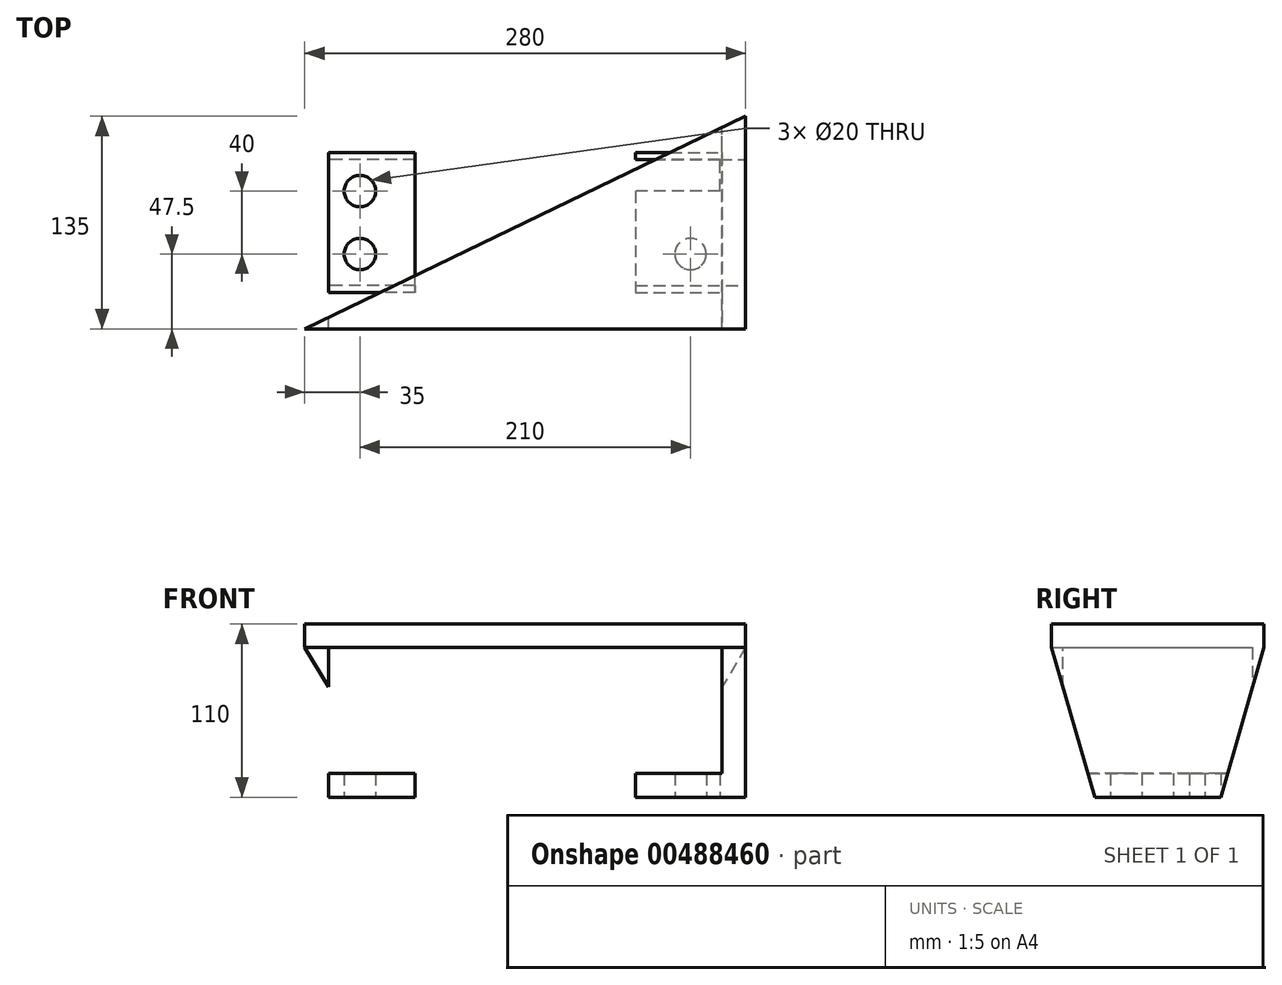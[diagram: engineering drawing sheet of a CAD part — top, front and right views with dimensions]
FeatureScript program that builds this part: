
annotation { "Feature Type Name" : "Feature", "Feature Type Description" : "" }
export const myFeature = defineFeature(function(context is Context, id is Id, definition is map)
    precondition{}
    {
        {
            var Q0;
            Q0=qCreatedBy(makeId("Top.planeOp"),FACE);
            var sketch = newSketch(context, id + "F0", { "sketchPlane" : qUnion([Q0])});
            skLineSegment(sketch, "E0", {"start": v(0, 0) * mm, "end": v(0, 135) * mm});
            skLineSegment(sketch, "E1", {"start": v(0, 135) * mm, "end": v(280, 135) * mm});
            skLineSegment(sketch, "E2", {"start": v(280, 135) * mm, "end": v(280, 0) * mm});
            skLineSegment(sketch, "E3", {"start": v(280, 0) * mm, "end": v(0, 0) * mm});
            skSolve(sketch);
        }
        {
            var Q0;
            Q0 = qSketchRegion(id + "F0", true);
            extrude(context, id + "F1", {"entities" : qUnion([Q0]), "depth" : 15 * mm});
        }
        {
            var Q0;
            Q0=makeQuery(id+"F1.opExtrude","SWEPT_FACE",FACE,{"disambiguationData":[OSD([sQuery(id+"F0.wireOp",EDGE,"E0")])]});
            var sketch = newSketch(context, id + "F2", { "sketchPlane" : qUnion([Q0])});
            skLineSegment(sketch, "E4", {"start": v(-135, 0) * mm, "end": v(0, 0) * mm});
            skLineSegment(sketch, "E5", {"start": v(-135, 15) * mm, "end": v(-166.77, 15) * mm});
            skLineSegment(sketch, "E6", {"start": v(-166.77, 15) * mm, "end": v(-166.77, -95) * mm});
            skLineSegment(sketch, "E7", {"start": v(-67.5, -95) * mm, "end": v(-27.5, -95) * mm});
            skLineSegment(sketch, "E8", {"start": v(-67.5, -95) * mm, "end": v(-107.5, -95) * mm});
            skLineSegment(sketch, "E9", {"start": v(-107.5, -95) * mm, "end": v(-135, 0) * mm});
            skLineSegment(sketch, "E10", {"start": v(-27.5, -95) * mm, "end": v(0, 0) * mm});
            skPoint(sketch, "E11.start.orphan", {"position": v(-67.5, 0) * mm});
            skSolve(sketch);
        }
        {
            var Q0;
            Q0 = qSketchRegion(id + "F2", true);
            extrude(context, id + "F3", {"entities" : qUnion([Q0]), "operationType" : NewBodyOperationType.ADD, "oppositeDirection" : true, "depth" : 15 * mm});
        }
        {
            var Q0;
            Q0=makeQuery(id+"F1.opExtrude","SWEPT_FACE",FACE,{"disambiguationData":[OSD([sQuery(id+"F0.wireOp",EDGE,"E2")])]});
            var sketch = newSketch(context, id + "F4", { "sketchPlane" : qUnion([Q0])});
            skLineSegment(sketch, "E12", {"start": v(0, 15) * mm, "end": v(-22.22, 15) * mm});
            skLineSegment(sketch, "E13", {"start": v(-22.22, 15) * mm, "end": v(-22.22, -95) * mm});
            skLineSegment(sketch, "E14", {"start": v(67.5, -95) * mm, "end": v(107.5, -95) * mm});
            skLineSegment(sketch, "E15", {"start": v(67.5, -95) * mm, "end": v(27.5, -95) * mm});
            skLineSegment(sketch, "E16", {"start": v(27.5, -95) * mm, "end": v(0, 0) * mm});
            skLineSegment(sketch, "E17", {"start": v(107.5, -95) * mm, "end": v(135, 0) * mm});
            skPoint(sketch, "E18.orphan", {"position": v(67.5, 0) * mm});
            skLineSegment(sketch, "E19", {"start": v(0, 0) * mm, "end": v(0, 15) * mm});
            skLineSegment(sketch, "E20", {"start": v(135, 15) * mm, "end": v(135, 0) * mm});
            skLineSegment(sketch, "E21", {"start": v(107.5, -95) * mm, "end": v(27.5, -95) * mm});
            skSolve(sketch);
        }
        {
            var Q0;
            Q0=makeQuery(id+"F4.imprint","IMPRINT",FACE,{"disambiguationData":[TD([[makeQuery(id+"F4.imprint","IMPRINT",EDGE,{"derivedFrom":sQuery(id+"F4.wireOp",EDGE,"E16")}),-1.0]])]});
            var Q1;
            Q1=makeQuery(id+"F4.imprint","IMPRINT",FACE,{"disambiguationData":[TD([[makeQuery(id+"F4.imprint","IMPRINT",EDGE,{"derivedFrom":sQuery(id+"F4.wireOp",EDGE,"E20")}),-1.0]])]});
            extrude(context, id + "F5", {"entities" : qUnion([Q0, Q1]), "operationType" : NewBodyOperationType.ADD, "oppositeDirection" : true, "depth" : 15 * mm});
        }
        {
            var Q0;
            Q0=makeQuery(id+"F1.opExtrude","CAP_FACE",FACE,{"disambiguationData":[OSD([sQuery(id+"F0.wireOp",EDGE,"E0"),sQuery(id+"F0.wireOp",EDGE,"E1"),sQuery(id+"F0.wireOp",EDGE,"E2"),sQuery(id+"F0.wireOp",EDGE,"E3")])],"isStart":false});
            var sketch = newSketch(context, id + "F6", { "sketchPlane" : qUnion([Q0])});
            skLineSegment(sketch, "E22", {"start": v(280, 0) * mm, "end": v(0, 135) * mm});
            skLineSegment(sketch, "E23", {"start": v(0, 135) * mm, "end": v(0, 0) * mm});
            skLineSegment(sketch, "E24", {"start": v(0, 0) * mm, "end": v(280, 135) * mm});
            skCircle(sketch, "E25", {"center": v(140, 67.5) * mm, "radius": 30 * mm});
            skSolve(sketch);
        }
        {
            var Q0;
            {var subQ0=sQuery(id+"F6.wireOp",EDGE,"E25");var subQ1=sQuery(id+"F6.wireOp",EDGE,"E22");var subQ2=makeQuery(id+"F6.imprint","INTERSECT",VERTEX,{"disambiguationData":[OD(0.0)],"derivedFrom":[subQ1,subQ0]});Q0=makeQuery(id+"F6.imprint","IMPRINT",FACE,{"disambiguationData":[TD([[makeQuery(id+"F6.imprint","IMPRINT",EDGE,{"disambiguationData":[TD([[subQ2,-1.0]])],"derivedFrom":subQ1}),1.0]])]});}
            var Q1;
            {var subQ0=sQuery(id+"F6.wireOp",EDGE,"E25");var subQ1=sQuery(id+"F6.wireOp",EDGE,"E22");var subQ2=makeQuery(id+"F6.imprint","INTERSECT",VERTEX,{"disambiguationData":[OD(0.0)],"derivedFrom":[subQ1,subQ0]});Q1=makeQuery(id+"F6.imprint","IMPRINT",FACE,{"disambiguationData":[TD([[makeQuery(id+"F6.imprint","IMPRINT",EDGE,{"disambiguationData":[TD([[subQ2,-1.0]])],"derivedFrom":subQ1}),-1.0]])]});}
            var Q2;
            {var subQ0=sQuery(id+"F6.wireOp",EDGE,"E24");var subQ1=sQuery(id+"F6.wireOp",EDGE,"E22");var subQ2=makeQuery(id+"F6.imprint","INTERSECT",VERTEX,{"derivedFrom":[subQ1,subQ0]});Q2=makeQuery(id+"F6.imprint","IMPRINT",FACE,{"disambiguationData":[TD([[makeQuery(id+"F6.imprint","IMPRINT",EDGE,{"disambiguationData":[TD([[subQ2,-1.0]])],"derivedFrom":subQ1}),1.0]])]});}
            var Q3;
            {var subQ0=sQuery(id+"F6.wireOp",EDGE,"E24");var subQ1=sQuery(id+"F6.wireOp",EDGE,"E22");var subQ2=makeQuery(id+"F6.imprint","INTERSECT",VERTEX,{"derivedFrom":[subQ1,subQ0]});Q3=makeQuery(id+"F6.imprint","IMPRINT",FACE,{"disambiguationData":[TD([[makeQuery(id+"F6.imprint","IMPRINT",EDGE,{"disambiguationData":[TD([[subQ2,-1.0]])],"derivedFrom":subQ1}),-1.0]])]});}
            extrude(context, id + "F7", {"entities" : qUnion([Q0, Q1, Q2, Q3]), "operationType" : NewBodyOperationType.REMOVE, "endBound" : BoundingType.THROUGH_ALL, "oppositeDirection" : true, "depth" : 25 * mm});
        }
        {
            var Q0;
            Q0=makeQuery(id+"F3.opExtrude","CAP_FACE",FACE,{"disambiguationData":[OSD([sQuery(id+"F2.wireOp",EDGE,"E4"),sQuery(id+"F2.wireOp",EDGE,"E7"),sQuery(id+"F2.wireOp",EDGE,"E8"),sQuery(id+"F2.wireOp",EDGE,"E9"),sQuery(id+"F2.wireOp",EDGE,"E10")])],"isStart":false});
            var sketch = newSketch(context, id + "F8", { "sketchPlane" : qUnion([Q0])});
            skLineSegment(sketch, "E26", {"start": v(27.5, -80) * mm, "end": v(111.84, -80) * mm});
            skLineSegment(sketch, "E27", {"start": v(111.84, -80) * mm, "end": v(23.16, -80) * mm});
            skLineSegment(sketch, "E28", {"start": v(27.5, -95) * mm, "end": v(23.16, -80) * mm});
            skLineSegment(sketch, "E29", {"start": v(27.5, -95) * mm, "end": v(107.5, -95) * mm});
            skLineSegment(sketch, "E30", {"start": v(107.5, -95) * mm, "end": v(111.84, -80) * mm});
            skSolve(sketch);
        }
        {
            var Q0;
            Q0 = qSketchRegion(id + "F8", true);
            extrude(context, id + "F9", {"entities" : qUnion([Q0]), "operationType" : NewBodyOperationType.ADD, "depth" : (70 - 15) * mm});
        }
        {
            var Q0;
            Q0=makeQuery(id+"F5.opExtrude","CAP_FACE",FACE,{"disambiguationData":[OSD([sQuery(id+"F0.wireOp",EDGE,"E2"),sQuery(id+"F4.wireOp",EDGE,"E16"),sQuery(id+"F4.wireOp",EDGE,"E17"),sQuery(id+"F4.wireOp",EDGE,"E20"),sQuery(id+"F4.wireOp",EDGE,"E21"),sQuery(id+"F4.wireOp",EDGE,"E19")])],"isStart":false});
            var sketch = newSketch(context, id + "F10", { "sketchPlane" : qUnion([Q0])});
            skLineSegment(sketch, "E31", {"start": v(-67.5, -95) * mm, "end": v(-67.5, -80) * mm});
            skLineSegment(sketch, "E32", {"start": v(-67.5, -80) * mm, "end": v(-23.16, -80) * mm});
            skLineSegment(sketch, "E33", {"start": v(-23.16, -80) * mm, "end": v(-111.84, -80) * mm});
            skLineSegment(sketch, "E34", {"start": v(-107.5, -95) * mm, "end": v(-27.5, -95) * mm});
            skLineSegment(sketch, "E35", {"start": v(-27.5, -95) * mm, "end": v(-23.16, -80) * mm});
            skLineSegment(sketch, "E36", {"start": v(-111.84, -80) * mm, "end": v(-107.5, -95) * mm});
            skSolve(sketch);
        }
        {
            var Q0;
            Q0 = qSketchRegion(id + "F10", true);
            extrude(context, id + "F11", {"entities" : qUnion([Q0]), "operationType" : NewBodyOperationType.ADD, "depth" : 55 * mm});
        }
        {
            var Q0;
            Q0=makeQuery(id+"F11.boolean.opBoolean","MERGE",FACE,{"derivedFrom":[makeQuery(id+"F5.opExtrude","SWEPT_FACE",FACE,{"disambiguationData":[OSD([sQuery(id+"F4.wireOp",EDGE,"E21")])]}),makeQuery(id+"F11.opExtrude","SWEPT_FACE",FACE,{"disambiguationData":[OSD([sQuery(id+"F10.wireOp",EDGE,"E34")])]})]});
            var sketch = newSketch(context, id + "F12", { "sketchPlane" : qUnion([Q0])});
            skLineSegment(sketch, "E37", {"start": v(210, -27.5) * mm, "end": v(280, -27.5) * mm});
            skLineSegment(sketch, "E38", {"start": v(245, -27.5) * mm, "end": v(245, -107.5) * mm});
            skLineSegment(sketch, "E39", {"start": v(245, -67.5) * mm, "end": v(263.69, -67.5) * mm});
            skLineSegment(sketch, "E40", {"start": v(263.69, -27.5) * mm, "end": v(263.69, -67.5) * mm});
            skLineSegment(sketch, "E41", {"start": v(263.69, -67.5) * mm, "end": v(263.69, -107.5) * mm});
            skLineSegment(sketch, "E42", {"start": v(263.69, -47.5) * mm, "end": v(0, -47.5) * mm});
            skLineSegment(sketch, "E43", {"start": v(263.69, -87.5) * mm, "end": v(0, -87.5) * mm});
            skLineSegment(sketch, "E44", {"start": v(280, -27.5) * mm, "end": v(0, -27.5) * mm});
            skLineSegment(sketch, "E45", {"start": v(0, -27.5) * mm, "end": v(0, -107.5) * mm});
            skLineSegment(sketch, "E46", {"start": v(0, -107.5) * mm, "end": v(70, -107.5) * mm});
            skLineSegment(sketch, "E47", {"start": v(35, -107.5) * mm, "end": v(35, -27.5) * mm});
            skCircle(sketch, "E48", {"center": v(245, -87.5) * mm, "radius": 10 * mm});
            skCircle(sketch, "E49", {"center": v(245, -47.5) * mm, "radius": 10 * mm});
            skCircle(sketch, "E50", {"center": v(35, -47.5) * mm, "radius": 10 * mm});
            skCircle(sketch, "E51", {"center": v(35, -87.5) * mm, "radius": 10 * mm});
            skSolve(sketch);
        }
        {
            var Q0;
            {var subQ0=sQuery(id+"F12.wireOp",EDGE,"E51");var subQ1=sQuery(id+"F12.wireOp",EDGE,"E43");var subQ2=makeQuery(id+"F12.imprint","INTERSECT",VERTEX,{"disambiguationData":[OD(0.0)],"derivedFrom":[subQ1,subQ0]});Q0=makeQuery(id+"F12.imprint","IMPRINT",FACE,{"disambiguationData":[TD([[makeQuery(id+"F12.imprint","IMPRINT",EDGE,{"disambiguationData":[TD([[subQ2,-1.0]])],"derivedFrom":subQ1}),1.0]])]});}
            var Q1;
            {var subQ0=sQuery(id+"F12.wireOp",EDGE,"E48");var subQ1=sQuery(id+"F12.wireOp",EDGE,"E38");var subQ2=makeQuery(id+"F12.imprint","INTERSECT",VERTEX,{"disambiguationData":[OD(0.0)],"derivedFrom":[subQ1,subQ0]});Q1=makeQuery(id+"F12.imprint","IMPRINT",FACE,{"disambiguationData":[TD([[makeQuery(id+"F12.imprint","IMPRINT",EDGE,{"disambiguationData":[TD([[subQ2,-1.0]])],"derivedFrom":subQ1}),1.0]])]});}
            var Q2;
            {var subQ0=sQuery(id+"F12.wireOp",EDGE,"E48");var subQ1=sQuery(id+"F12.wireOp",EDGE,"E38");var subQ2=makeQuery(id+"F12.imprint","INTERSECT",VERTEX,{"disambiguationData":[OD(0.0)],"derivedFrom":[subQ1,subQ0]});Q2=makeQuery(id+"F12.imprint","IMPRINT",FACE,{"disambiguationData":[TD([[makeQuery(id+"F12.imprint","IMPRINT",EDGE,{"disambiguationData":[TD([[subQ2,-1.0]])],"derivedFrom":subQ1}),-1.0]])]});}
            var Q3;
            {var subQ0=sQuery(id+"F12.wireOp",EDGE,"E43");var subQ1=sQuery(id+"F12.wireOp",EDGE,"E38");var subQ2=makeQuery(id+"F12.imprint","INTERSECT",VERTEX,{"derivedFrom":[subQ1,subQ0]});Q3=makeQuery(id+"F12.imprint","IMPRINT",FACE,{"disambiguationData":[TD([[makeQuery(id+"F12.imprint","IMPRINT",EDGE,{"disambiguationData":[TD([[subQ2,-1.0]])],"derivedFrom":subQ1}),1.0]])]});}
            var Q4;
            {var subQ0=sQuery(id+"F12.wireOp",EDGE,"E43");var subQ1=sQuery(id+"F12.wireOp",EDGE,"E38");var subQ2=makeQuery(id+"F12.imprint","INTERSECT",VERTEX,{"derivedFrom":[subQ1,subQ0]});Q4=makeQuery(id+"F12.imprint","IMPRINT",FACE,{"disambiguationData":[TD([[makeQuery(id+"F12.imprint","IMPRINT",EDGE,{"disambiguationData":[TD([[subQ2,-1.0]])],"derivedFrom":subQ1}),-1.0]])]});}
            var Q5;
            {var subQ0=sQuery(id+"F12.wireOp",EDGE,"E51");var subQ1=sQuery(id+"F12.wireOp",EDGE,"E43");var subQ2=makeQuery(id+"F12.imprint","INTERSECT",VERTEX,{"disambiguationData":[OD(0.0)],"derivedFrom":[subQ1,subQ0]});Q5=makeQuery(id+"F12.imprint","IMPRINT",FACE,{"disambiguationData":[TD([[makeQuery(id+"F12.imprint","IMPRINT",EDGE,{"disambiguationData":[TD([[subQ2,-1.0]])],"derivedFrom":subQ1}),-1.0]])]});}
            var Q6;
            {var subQ0=sQuery(id+"F12.wireOp",EDGE,"E47");var subQ1=sQuery(id+"F12.wireOp",EDGE,"E43");var subQ2=makeQuery(id+"F12.imprint","INTERSECT",VERTEX,{"derivedFrom":[subQ1,subQ0]});Q6=makeQuery(id+"F12.imprint","IMPRINT",FACE,{"disambiguationData":[TD([[makeQuery(id+"F12.imprint","IMPRINT",EDGE,{"disambiguationData":[TD([[subQ2,-1.0]])],"derivedFrom":subQ1}),1.0]])]});}
            var Q7;
            {var subQ0=sQuery(id+"F12.wireOp",EDGE,"E47");var subQ1=sQuery(id+"F12.wireOp",EDGE,"E43");var subQ2=makeQuery(id+"F12.imprint","INTERSECT",VERTEX,{"derivedFrom":[subQ1,subQ0]});Q7=makeQuery(id+"F12.imprint","IMPRINT",FACE,{"disambiguationData":[TD([[makeQuery(id+"F12.imprint","IMPRINT",EDGE,{"disambiguationData":[TD([[subQ2,-1.0]])],"derivedFrom":subQ1}),-1.0]])]});}
            var Q8;
            {var subQ0=sQuery(id+"F12.wireOp",EDGE,"E50");var subQ1=sQuery(id+"F12.wireOp",EDGE,"E42");var subQ2=makeQuery(id+"F12.imprint","INTERSECT",VERTEX,{"disambiguationData":[OD(0.0)],"derivedFrom":[subQ1,subQ0]});Q8=makeQuery(id+"F12.imprint","IMPRINT",FACE,{"disambiguationData":[TD([[makeQuery(id+"F12.imprint","IMPRINT",EDGE,{"disambiguationData":[TD([[subQ2,-1.0]])],"derivedFrom":subQ1}),1.0]])]});}
            var Q9;
            {var subQ0=sQuery(id+"F12.wireOp",EDGE,"E47");var subQ1=sQuery(id+"F12.wireOp",EDGE,"E42");var subQ2=makeQuery(id+"F12.imprint","INTERSECT",VERTEX,{"derivedFrom":[subQ1,subQ0]});Q9=makeQuery(id+"F12.imprint","IMPRINT",FACE,{"disambiguationData":[TD([[makeQuery(id+"F12.imprint","IMPRINT",EDGE,{"disambiguationData":[TD([[subQ2,-1.0]])],"derivedFrom":subQ1}),1.0]])]});}
            var Q10;
            {var subQ0=sQuery(id+"F12.wireOp",EDGE,"E47");var subQ1=sQuery(id+"F12.wireOp",EDGE,"E42");var subQ2=makeQuery(id+"F12.imprint","INTERSECT",VERTEX,{"derivedFrom":[subQ1,subQ0]});Q10=makeQuery(id+"F12.imprint","IMPRINT",FACE,{"disambiguationData":[TD([[makeQuery(id+"F12.imprint","IMPRINT",EDGE,{"disambiguationData":[TD([[subQ2,-1.0]])],"derivedFrom":subQ1}),-1.0]])]});}
            var Q11;
            {var subQ0=sQuery(id+"F12.wireOp",EDGE,"E50");var subQ1=sQuery(id+"F12.wireOp",EDGE,"E42");var subQ2=makeQuery(id+"F12.imprint","INTERSECT",VERTEX,{"disambiguationData":[OD(0.0)],"derivedFrom":[subQ1,subQ0]});Q11=makeQuery(id+"F12.imprint","IMPRINT",FACE,{"disambiguationData":[TD([[makeQuery(id+"F12.imprint","IMPRINT",EDGE,{"disambiguationData":[TD([[subQ2,-1.0]])],"derivedFrom":subQ1}),-1.0]])]});}
            var Q12;
            {var subQ0=sQuery(id+"F12.wireOp",EDGE,"E42");var subQ1=sQuery(id+"F12.wireOp",EDGE,"E38");var subQ2=makeQuery(id+"F12.imprint","INTERSECT",VERTEX,{"derivedFrom":[subQ1,subQ0]});Q12=makeQuery(id+"F12.imprint","IMPRINT",FACE,{"disambiguationData":[TD([[makeQuery(id+"F12.imprint","IMPRINT",EDGE,{"disambiguationData":[TD([[subQ2,-1.0]])],"derivedFrom":subQ1}),-1.0]])]});}
            var Q13;
            {var subQ0=sQuery(id+"F12.wireOp",EDGE,"E42");var subQ1=sQuery(id+"F12.wireOp",EDGE,"E38");var subQ2=makeQuery(id+"F12.imprint","INTERSECT",VERTEX,{"derivedFrom":[subQ1,subQ0]});Q13=makeQuery(id+"F12.imprint","IMPRINT",FACE,{"disambiguationData":[TD([[makeQuery(id+"F12.imprint","IMPRINT",EDGE,{"disambiguationData":[TD([[subQ2,-1.0]])],"derivedFrom":subQ1}),1.0]])]});}
            var Q14;
            {var subQ0=sQuery(id+"F12.wireOp",EDGE,"E49");var subQ1=sQuery(id+"F12.wireOp",EDGE,"E38");var subQ2=makeQuery(id+"F12.imprint","INTERSECT",VERTEX,{"disambiguationData":[OD(0.0)],"derivedFrom":[subQ1,subQ0]});Q14=makeQuery(id+"F12.imprint","IMPRINT",FACE,{"disambiguationData":[TD([[makeQuery(id+"F12.imprint","IMPRINT",EDGE,{"disambiguationData":[TD([[subQ2,-1.0]])],"derivedFrom":subQ1}),1.0]])]});}
            var Q15;
            {var subQ0=sQuery(id+"F12.wireOp",EDGE,"E49");var subQ1=sQuery(id+"F12.wireOp",EDGE,"E38");var subQ2=makeQuery(id+"F12.imprint","INTERSECT",VERTEX,{"disambiguationData":[OD(0.0)],"derivedFrom":[subQ1,subQ0]});Q15=makeQuery(id+"F12.imprint","IMPRINT",FACE,{"disambiguationData":[TD([[makeQuery(id+"F12.imprint","IMPRINT",EDGE,{"disambiguationData":[TD([[subQ2,-1.0]])],"derivedFrom":subQ1}),-1.0]])]});}
            extrude(context, id + "F13", {"entities" : qUnion([Q0, Q1, Q2, Q3, Q4, Q5, Q6, Q7, Q8, Q9, Q10, Q11, Q12, Q13, Q14, Q15]), "operationType" : NewBodyOperationType.REMOVE, "oppositeDirection" : true, "depth" : 25 * mm});
        }
    });
